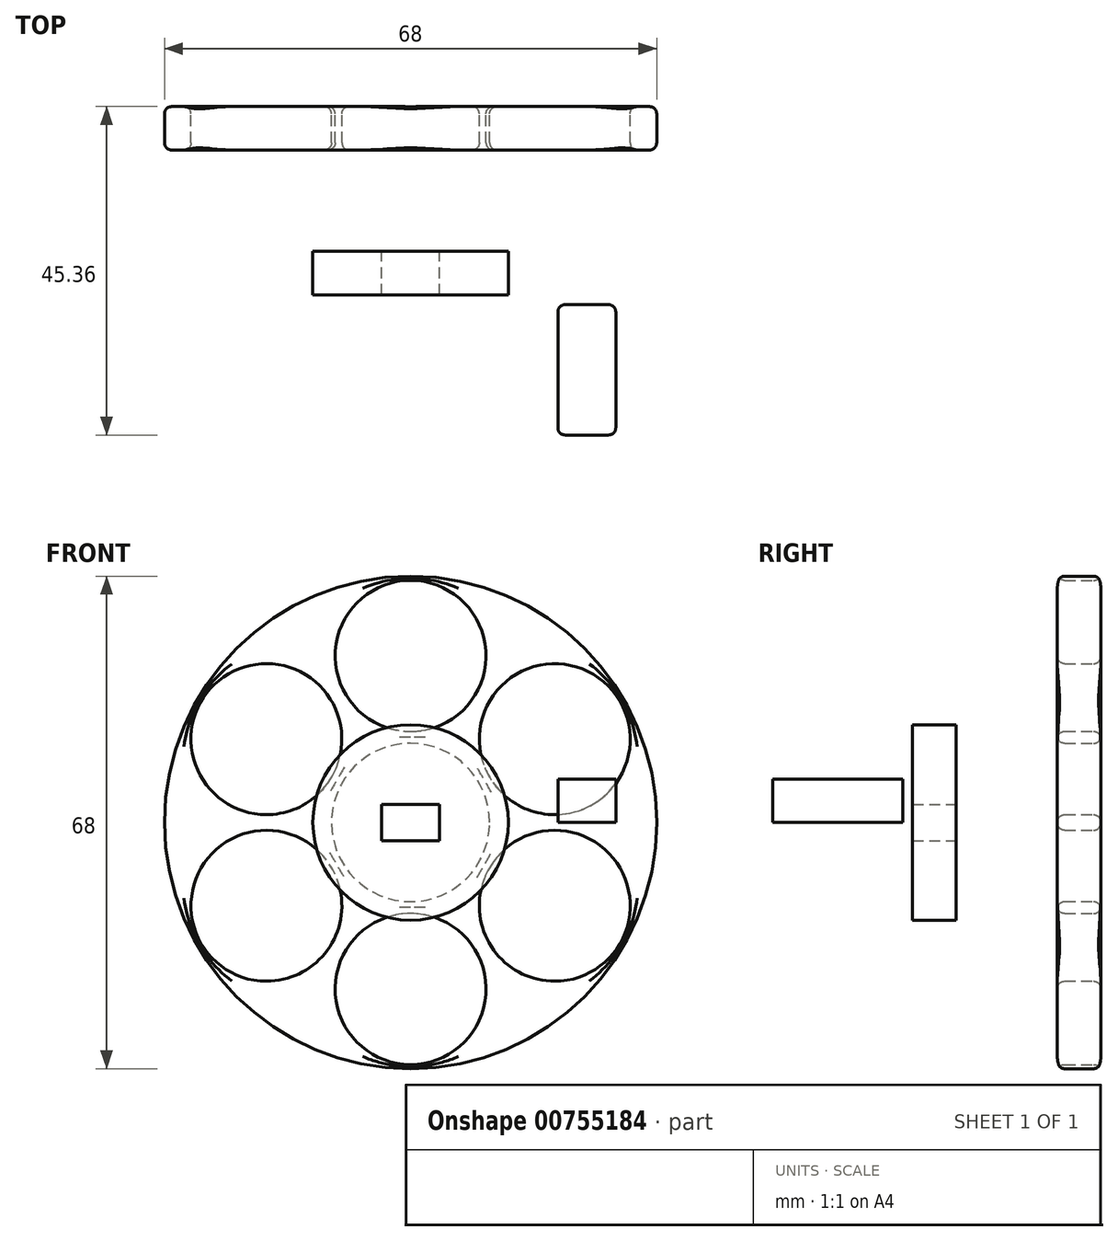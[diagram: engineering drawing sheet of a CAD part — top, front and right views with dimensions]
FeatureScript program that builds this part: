
annotation { "Feature Type Name" : "Feature", "Feature Type Description" : "" }
export const myFeature = defineFeature(function(context is Context, id is Id, definition is map)
    precondition{}
    {
        {
            var Q0;
            Q0=qCreatedBy(makeId("Front.planeOp"),FACE);
            var sketch = newSketch(context, id + "F0", { "sketchPlane" : qUnion([Q0])});
            skCircle(sketch, "E0", {"center": v(0, 0) * mm, "radius": 10.93 * mm});
            skCircle(sketch, "E1", {"center": v(0, 23) * mm, "radius": 10.43 * mm});
            skCircle(sketch, "E2.1.0", {"center": v(-19.92, 11.5) * mm, "radius": 10.43 * mm});
            skCircle(sketch, "E2.2.0", {"center": v(-19.92, -11.5) * mm, "radius": 10.43 * mm});
            skCircle(sketch, "E2.3.0", {"center": v(0, -23) * mm, "radius": 10.43 * mm});
            skCircle(sketch, "E2.4.0", {"center": v(19.92, -11.5) * mm, "radius": 10.43 * mm});
            skCircle(sketch, "E2.5.0", {"center": v(19.92, 11.5) * mm, "radius": 10.43 * mm});
            skCircle(sketch, "E3", {"center": v(0, 0) * mm, "radius": 34 * mm});
            skSolve(sketch);
        }
        {
            var Q0;
            Q0=makeQuery(id+"F0.imprint","IMPRINT",FACE,{"disambiguationData":[TD([[makeQuery(id+"F0.imprint","IMPRINT",EDGE,{"derivedFrom":sQuery(id+"F0.wireOp",EDGE,"E0")}),-1.0]])]});
            var Q1;
            {var subQ4=sQuery(id+"F0.wireOp",EDGE,"927991e9-9f71-4b2e-be31-a3cea801bfd6.trimOffspring");Q1=makeQuery(id+"F0.imprint","IMPRINT",FACE,{"disambiguationData":[TD([[makeQuery(id+"F0.imprint","IMPRINT",EDGE,{"derivedFrom":subQ4}),-1.0]])]});}
            var Q2;
            {var subQ1=sQuery(id+"F0.wireOp",EDGE,"81e7d2ae-2a3f-4248-a7e5-f6c1022807f2.2.0");Q2=makeQuery(id+"F0.imprint","IMPRINT",FACE,{"disambiguationData":[TD([[makeQuery(id+"F0.imprint","IMPRINT",EDGE,{"derivedFrom":subQ1}),1.0]])]});}
            var Q3;
            {var subQ1=sQuery(id+"F0.wireOp",EDGE,"520c5b3a-aa43-4f06-9555-10364a7817d5.trimOffspring");Q3=makeQuery(id+"F0.imprint","IMPRINT",FACE,{"disambiguationData":[TD([[makeQuery(id+"F0.imprint","IMPRINT",EDGE,{"derivedFrom":subQ1}),-1.0]])]});}
            var Q4;
            {var subQ2=sQuery(id+"F0.wireOp",EDGE,"vsBpCTxl-7o5t-uiH5-LdrU-oTl888prj2Ty");Q4=makeQuery(id+"F0.imprint","IMPRINT",FACE,{"disambiguationData":[TD([[makeQuery(id+"F0.imprint","IMPRINT",EDGE,{"derivedFrom":subQ2}),-1.0]])]});}
            var Q5;
            {var subQ0=sQuery(id+"F0.wireOp",EDGE,"af0ad528-bc79-4a57-b356-ea0f640c4d19.filletArc");Q5=makeQuery(id+"F0.imprint","IMPRINT",FACE,{"disambiguationData":[TD([[makeQuery(id+"F0.imprint","IMPRINT",EDGE,{"derivedFrom":subQ0}),1.0]])]});}
            var Q6;
            {var subQ0=sQuery(id+"F0.wireOp",EDGE,"d15f818b-7e05-4279-b62b-b2b877da8790.filletArc");Q6=makeQuery(id+"F0.imprint","IMPRINT",FACE,{"disambiguationData":[TD([[makeQuery(id+"F0.imprint","IMPRINT",EDGE,{"derivedFrom":subQ0}),1.0]])]});}
            extrude(context, id + "F1", {"entities" : qUnion([Q0, Q1, Q2, Q3, Q4, Q5, Q6]), "depth" : 6 * mm, "offsetDistance" : 25 * mm});
        }
        {
            var Q0;
            Q0=makeQuery(id+"F1.opExtrude","CAP_FACE",FACE,{"disambiguationData":[OSD([sQuery(id+"F0.wireOp",EDGE,"E0"),sQuery(id+"F0.wireOp",EDGE,"WUNrHDuF-X21H-M96y-Lme7-B8YP7Xxl3z8T"),sQuery(id+"F0.wireOp",EDGE,"6345f1c2-771f-4573-b072-38c9fe25f44f.1.0"),sQuery(id+"F0.wireOp",EDGE,"6345f1c2-771f-4573-b072-38c9fe25f44f.2.0"),sQuery(id+"F0.wireOp",EDGE,"6345f1c2-771f-4573-b072-38c9fe25f44f.3.0"),sQuery(id+"F0.wireOp",EDGE,"6345f1c2-771f-4573-b072-38c9fe25f44f.4.0"),sQuery(id+"F0.wireOp",EDGE,"6w4LuyIg-Judz-7qcx-iNhM-kCVs0XRHMAQz.left"),sQuery(id+"F0.wireOp",EDGE,"6w4LuyIg-Judz-7qcx-iNhM-kCVs0XRHMAQz.right"),sQuery(id+"F0.wireOp",EDGE,"GuxD1Two-tXSI-jhGi-diOq-QsG6SmieNdRW"),sQuery(id+"F0.wireOp",EDGE,"9e989a9f-be13-4d0f-822f-95c7c0624428.1.0"),sQuery(id+"F0.wireOp",EDGE,"9e989a9f-be13-4d0f-822f-95c7c0624428.1.1"),sQuery(id+"F0.wireOp",EDGE,"9e989a9f-be13-4d0f-822f-95c7c0624428.1.2"),sQuery(id+"F0.wireOp",EDGE,"9e989a9f-be13-4d0f-822f-95c7c0624428.2.0"),sQuery(id+"F0.wireOp",EDGE,"9e989a9f-be13-4d0f-822f-95c7c0624428.2.1"),sQuery(id+"F0.wireOp",EDGE,"9e989a9f-be13-4d0f-822f-95c7c0624428.2.2"),sQuery(id+"F0.wireOp",EDGE,"9e989a9f-be13-4d0f-822f-95c7c0624428.3.0"),sQuery(id+"F0.wireOp",EDGE,"9e989a9f-be13-4d0f-822f-95c7c0624428.3.1"),sQuery(id+"F0.wireOp",EDGE,"9e989a9f-be13-4d0f-822f-95c7c0624428.3.2"),sQuery(id+"F0.wireOp",EDGE,"9e989a9f-be13-4d0f-822f-95c7c0624428.4.0"),sQuery(id+"F0.wireOp",EDGE,"9e989a9f-be13-4d0f-822f-95c7c0624428.4.1"),sQuery(id+"F0.wireOp",EDGE,"9e989a9f-be13-4d0f-822f-95c7c0624428.4.2"),sQuery(id+"F0.wireOp",EDGE,"486a15bc-75c9-41d0-808c-e5c4775e6e80.filletArc"),sQuery(id+"F0.wireOp",EDGE,"d314a861-2769-46d2-9bec-117903992242.filletArc"),sQuery(id+"F0.wireOp",EDGE,"5d220be9-c9be-4508-b7a3-f434c5fdea58.filletArc"),sQuery(id+"F0.wireOp",EDGE,"2974d6c2-e4a2-45df-9bc2-224e587c2884.filletArc"),sQuery(id+"F0.wireOp",EDGE,"3265ed39-f9f2-4246-9e43-8a9d8c4dec78.filletArc")])],"isStart":false});
            var Q1;
            Q1=makeQuery(id+"F1.opExtrude","CAP_FACE",FACE,{"disambiguationData":[OSD([sQuery(id+"F0.wireOp",EDGE,"E0"),sQuery(id+"F0.wireOp",EDGE,"WUNrHDuF-X21H-M96y-Lme7-B8YP7Xxl3z8T"),sQuery(id+"F0.wireOp",EDGE,"6345f1c2-771f-4573-b072-38c9fe25f44f.1.0"),sQuery(id+"F0.wireOp",EDGE,"6345f1c2-771f-4573-b072-38c9fe25f44f.2.0"),sQuery(id+"F0.wireOp",EDGE,"6345f1c2-771f-4573-b072-38c9fe25f44f.3.0"),sQuery(id+"F0.wireOp",EDGE,"6345f1c2-771f-4573-b072-38c9fe25f44f.4.0"),sQuery(id+"F0.wireOp",EDGE,"6w4LuyIg-Judz-7qcx-iNhM-kCVs0XRHMAQz.left"),sQuery(id+"F0.wireOp",EDGE,"6w4LuyIg-Judz-7qcx-iNhM-kCVs0XRHMAQz.right"),sQuery(id+"F0.wireOp",EDGE,"GuxD1Two-tXSI-jhGi-diOq-QsG6SmieNdRW"),sQuery(id+"F0.wireOp",EDGE,"9e989a9f-be13-4d0f-822f-95c7c0624428.1.0"),sQuery(id+"F0.wireOp",EDGE,"9e989a9f-be13-4d0f-822f-95c7c0624428.1.1"),sQuery(id+"F0.wireOp",EDGE,"9e989a9f-be13-4d0f-822f-95c7c0624428.1.2"),sQuery(id+"F0.wireOp",EDGE,"9e989a9f-be13-4d0f-822f-95c7c0624428.2.0"),sQuery(id+"F0.wireOp",EDGE,"9e989a9f-be13-4d0f-822f-95c7c0624428.2.1"),sQuery(id+"F0.wireOp",EDGE,"9e989a9f-be13-4d0f-822f-95c7c0624428.2.2"),sQuery(id+"F0.wireOp",EDGE,"9e989a9f-be13-4d0f-822f-95c7c0624428.3.0"),sQuery(id+"F0.wireOp",EDGE,"9e989a9f-be13-4d0f-822f-95c7c0624428.3.1"),sQuery(id+"F0.wireOp",EDGE,"9e989a9f-be13-4d0f-822f-95c7c0624428.3.2"),sQuery(id+"F0.wireOp",EDGE,"9e989a9f-be13-4d0f-822f-95c7c0624428.4.0"),sQuery(id+"F0.wireOp",EDGE,"9e989a9f-be13-4d0f-822f-95c7c0624428.4.1"),sQuery(id+"F0.wireOp",EDGE,"9e989a9f-be13-4d0f-822f-95c7c0624428.4.2"),sQuery(id+"F0.wireOp",EDGE,"486a15bc-75c9-41d0-808c-e5c4775e6e80.filletArc"),sQuery(id+"F0.wireOp",EDGE,"d314a861-2769-46d2-9bec-117903992242.filletArc"),sQuery(id+"F0.wireOp",EDGE,"5d220be9-c9be-4508-b7a3-f434c5fdea58.filletArc"),sQuery(id+"F0.wireOp",EDGE,"2974d6c2-e4a2-45df-9bc2-224e587c2884.filletArc"),sQuery(id+"F0.wireOp",EDGE,"3265ed39-f9f2-4246-9e43-8a9d8c4dec78.filletArc")])],"isStart":true});
            fillet(context, id + "F2", {"entities" : qUnion([Q0, Q1]), "radius" : 1 * mm, "tangentPropagation" : true, "allowEdgeOverflow" : false});
        }
        {
            var Q0;
            Q0=qCreatedBy(makeId("Top.planeOp"),FACE);
            var sketch = newSketch(context, id + "F3", { "sketchPlane" : qUnion([Q0])});
            skLineSegment(sketch, "E4.bottom", {"start": v(21.35, -27.36) * mm, "end": v(27.35, -27.36) * mm});
            skLineSegment(sketch, "E4.top", {"start": v(21.35, -45.36) * mm, "end": v(27.35, -45.36) * mm});
            skLineSegment(sketch, "E4.left", {"start": v(20.35, -28.36) * mm, "end": v(20.35, -44.36) * mm});
            skLineSegment(sketch, "E4.right", {"start": v(28.35, -28.36) * mm, "end": v(28.35, -44.36) * mm});
            skPoint(sketch, "E4.middle", {"position": v(24.35, -36.36) * mm});
            skPoint(sketch, "E5.visualSharp", {"position": v(20.35, -45.36) * mm});
            skArc(sketch, "E5.filletArc", {"start": v(20.35, -44.36) * mm, "mid": v(20.64, -45.06) * mm, "end": v(21.35, -45.36) * mm});
            skPoint(sketch, "E6.visualSharp", {"position": v(28.35, -45.36) * mm});
            skArc(sketch, "E6.filletArc", {"start": v(27.35, -45.36) * mm, "mid": v(28.05, -45.06) * mm, "end": v(28.35, -44.36) * mm});
            skPoint(sketch, "E7.visualSharp", {"position": v(28.35, -27.36) * mm});
            skArc(sketch, "E7.filletArc", {"start": v(28.35, -28.36) * mm, "mid": v(28.05, -27.65) * mm, "end": v(27.35, -27.36) * mm});
            skPoint(sketch, "E8.visualSharp", {"position": v(20.35, -27.36) * mm});
            skArc(sketch, "E8.filletArc", {"start": v(21.35, -27.36) * mm, "mid": v(20.64, -27.65) * mm, "end": v(20.35, -28.36) * mm});
            skSolve(sketch);
        }
        {
            var Q0;
            Q0=makeQuery(id+"F3.imprint","IMPRINT",FACE,{"disambiguationData":[TD([[makeQuery(id+"F3.imprint","IMPRINT",EDGE,{"derivedFrom":sQuery(id+"F3.wireOp",EDGE,"E4.bottom")}),-1.0]])]});
            extrude(context, id + "F4", {"entities" : qUnion([Q0]), "depth" : 6 * mm, "offsetDistance" : 25 * mm});
        }
        {
            var Q0;
            Q0=qCreatedBy(makeId("Front.planeOp"),FACE);
            var sketch = newSketch(context, id + "F5", { "sketchPlane" : qUnion([Q0])});
            skCircle(sketch, "E9", {"center": v(0, 0) * mm, "radius": 13.5 * mm});
            skLineSegment(sketch, "E10.bottom", {"start": v(4, -2.5) * mm, "end": v(-4, -2.5) * mm});
            skLineSegment(sketch, "E10.top", {"start": v(4, 2.5) * mm, "end": v(-4, 2.5) * mm});
            skLineSegment(sketch, "E10.left", {"start": v(4, -2.5) * mm, "end": v(4, 2.5) * mm});
            skLineSegment(sketch, "E10.right", {"start": v(-4, -2.5) * mm, "end": v(-4, 2.5) * mm});
            skSolve(sketch);
        }
        {
            var Q0;
            Q0=qSketchRegion(id+"F5",true);
            extrude(context, id + "F6", {"entities" : qUnion([Q0]), "depth" : 26 * mm, "offsetDistance" : 25 * mm, "hasSecondDirection" : true, "secondDirectionOppositeDirection" : false, "secondDirectionDepth" : 20 * mm});
        }
    });
